# Revit family: PieuVistech
name_source: partatom
category: Fondations
revit_build: Autodesk Revit 2017 (Build: 20160606_1515(x64)
units: mm (PartAtom-declared; Revit-internal decimal feet)

## family parameters
Couper avec des vides une fois chargée = Non
Couronne = Non
Hôte = Face
Matériau pour le comportement du modèle = Acier
Partagée = Non

## types (6) — shared parameters
Elévation par défaut = 48"
ØSymbole = 6 1/2"
ΔAilette = 4 1/2"
ΔTrou = 3"
εAilette = 1/2"

## per-type parameters (varying)
| type | ØAilette | ØExt | ØInt | ΔSymbole | ρAilette | яAilette |
| PieuVistech | 20" | 3 1/2" | 3 9/128" | 12" | 115 1/2" | 1 3/4" |
| PieuVistech Bleu | 24" | 4" | 3 35/64" | 0" | 175 1/8" | 2" |
| PieuVistech Rose | 24" | 4" | 3 35/64" | 0" | 173 1/8" | 2" |
| PieuVistech Mauve | 24" | 4" | 3 35/64" | 0" | 183 1/4" | 2" |
| PieuVistech Vert | 24" | 4" | 3 35/64" | 0" | 157" | 2" |
| Pieu iso | 24" | 3 1/2" | 3 9/128" | 12" | 79 1/2" | 1 3/4" |

## geometry (parser evidence)
native form markers: Blend x4
no freeform markers — native parametric forms only
